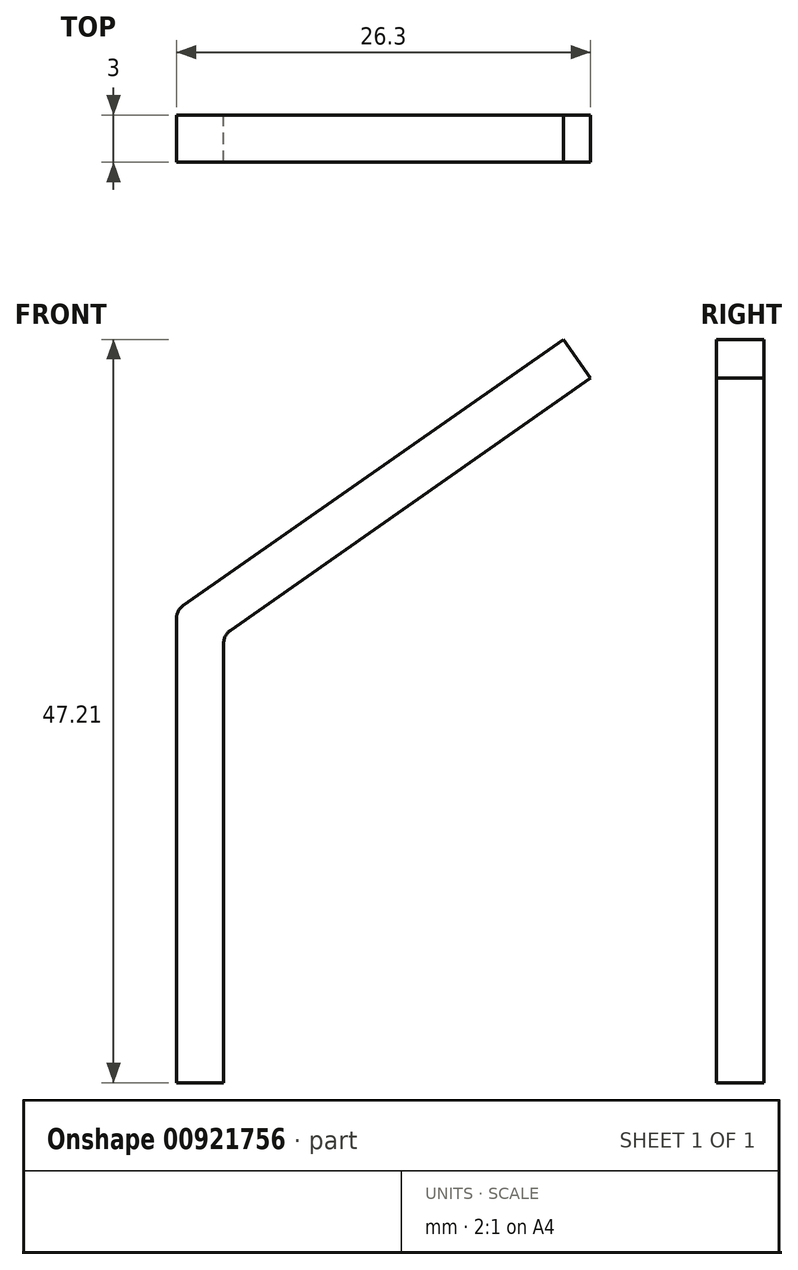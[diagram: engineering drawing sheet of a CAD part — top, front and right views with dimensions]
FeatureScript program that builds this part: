
annotation { "Feature Type Name" : "Feature", "Feature Type Description" : "" }
export const myFeature = defineFeature(function(context is Context, id is Id, definition is map)
    precondition{}
    {
        {
            var Q0;
            Q0=qCreatedBy(makeId("Front.planeOp"),FACE);
            var sketch = newSketch(context, id + "F0", { "sketchPlane" : qUnion([Q0])});
            skLineSegment(sketch, "E0.bottom", {"start": v(0, 0) * mm, "end": v(3, 0) * mm});
            skLineSegment(sketch, "E0.top", {"start": v(0, 30) * mm, "end": v(3, 30) * mm});
            skLineSegment(sketch, "E0.left", {"start": v(0, 0) * mm, "end": v(0, 30) * mm});
            skLineSegment(sketch, "E0.right", {"start": v(3, 0) * mm, "end": v(3, 30) * mm});
            skLineSegment(sketch, "E1", {"start": v(0, 30) * mm, "end": v(24.57, 47.2) * mm});
            skLineSegment(sketch, "E2", {"start": v(24.57, 47.2) * mm, "end": v(26.3, 44.75) * mm});
            skLineSegment(sketch, "E3", {"start": v(26.3, 44.75) * mm, "end": v(1.72, 27.54) * mm});
            skLineSegment(sketch, "E4", {"start": v(1.72, 27.54) * mm, "end": v(0, 30) * mm});
            skSolve(sketch);
        }
        {
            var Q0;
            {var subQ4=sQuery(id+"F0.wireOp",EDGE,"E0.bottom");Q0=makeQuery(id+"F0.imprint","IMPRINT",FACE,{"disambiguationData":[TD([[makeQuery(id+"F0.imprint","IMPRINT",EDGE,{"derivedFrom":subQ4}),1.0]])]});}
            var Q1;
            {var subQ0=sQuery(id+"F0.wireOp",EDGE,"E0.top");Q1=makeQuery(id+"F0.imprint","IMPRINT",FACE,{"disambiguationData":[TD([[makeQuery(id+"F0.imprint","IMPRINT",EDGE,{"derivedFrom":subQ0}),-1.0]])]});}
            var Q2;
            {var subQ1=sQuery(id+"F0.wireOp",EDGE,"E0.top");Q2=makeQuery(id+"F0.imprint","IMPRINT",FACE,{"disambiguationData":[TD([[makeQuery(id+"F0.imprint","IMPRINT",EDGE,{"derivedFrom":subQ1}),1.0]])]});}
            extrude(context, id + "F1", {"entities" : qUnion([Q0, Q1, Q2]), "depth" : 3 * mm, "offsetDistance" : 25 * mm});
        }
        {
            var Q0;
            Q0=makeQuery(id+"F1.opExtrude","SWEPT_EDGE",EDGE,{"disambiguationData":[OSD([sQuery(id+"F0.wireOp",EDGE,"E0.top"),sQuery(id+"F0.wireOp",EDGE,"E0.left"),sQuery(id+"F0.wireOp",EDGE,"E1"),sQuery(id+"F0.wireOp",EDGE,"E4")])]});
            var Q1;
            Q1=makeQuery(id+"F1.opExtrude","SWEPT_EDGE",EDGE,{"disambiguationData":[OSD([sQuery(id+"F0.wireOp",EDGE,"E0.right"),sQuery(id+"F0.wireOp",EDGE,"E3")])]});
            fillet(context, id + "F2", {"entities" : qUnion([Q0, Q1]), "radius" : 1 * mm, "tangentPropagation" : true, "allowEdgeOverflow" : false});
        }
    });
